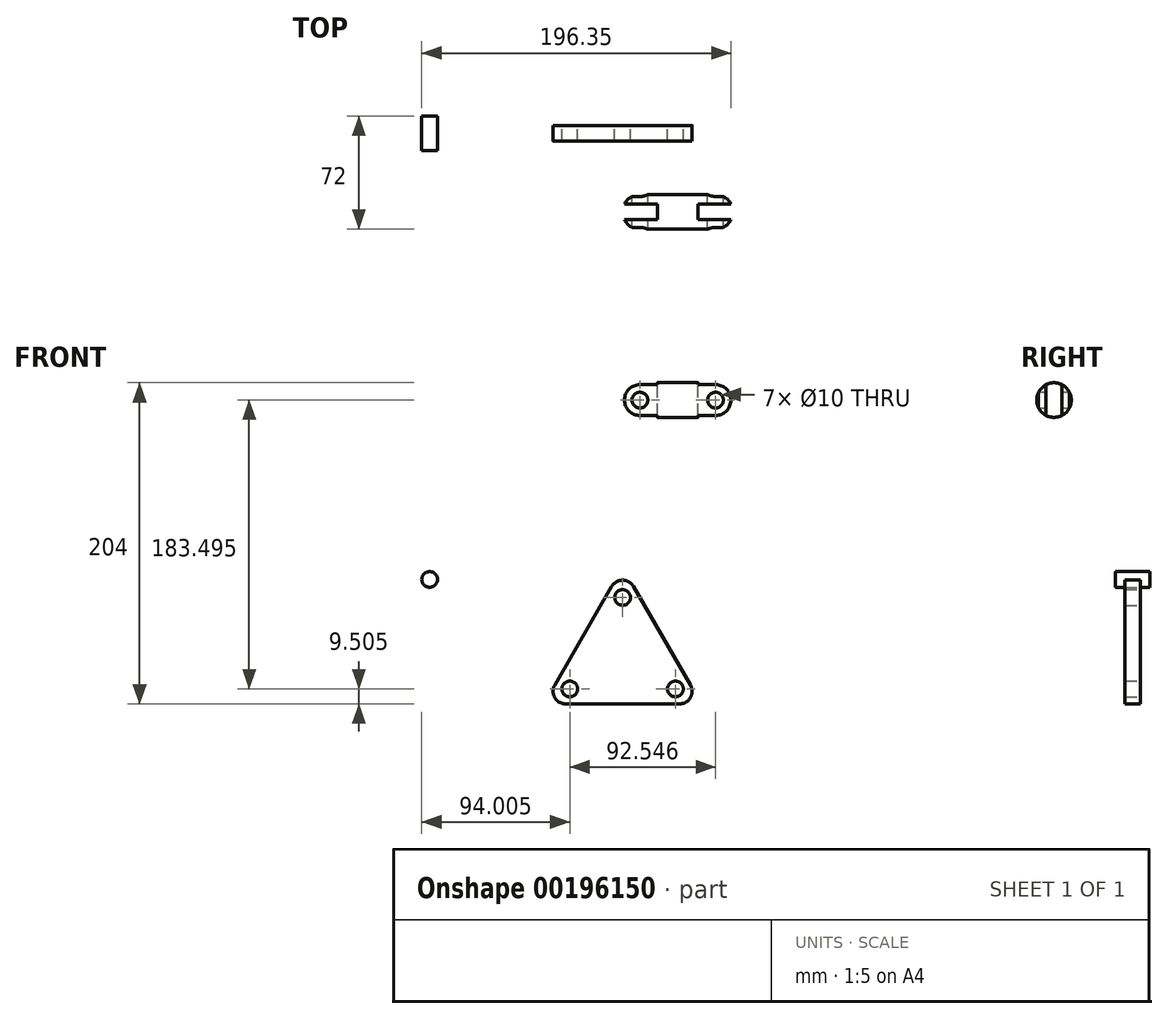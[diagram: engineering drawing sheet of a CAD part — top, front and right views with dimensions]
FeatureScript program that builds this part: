
annotation { "Feature Type Name" : "Feature", "Feature Type Description" : "" }
export const myFeature = defineFeature(function(context is Context, id is Id, definition is map)
    precondition{}
    {
        {
            var Q0;
            Q0=qCreatedBy(makeId("Front.planeOp"),FACE);
            var sketch = newSketch(context, id + "F0", { "sketchPlane" : qUnion([Q0])});
            skLineSegment(sketch, "E0", {"start": v(-36.14, -43) * mm, "end": v(36.14, -43) * mm});
            skLineSegment(sketch, "E1", {"start": v(43.07, -31) * mm, "end": v(6.93, 31.6) * mm});
            skLineSegment(sketch, "E2", {"start": v(-6.93, 31.6) * mm, "end": v(-43.07, -31) * mm});
            skCircle(sketch, "E3", {"center": v(0, 24.6) * mm, "radius": 5 * mm});
            skCircle(sketch, "E4", {"center": v(33.55, -33.5) * mm, "radius": 5 * mm});
            skCircle(sketch, "E5", {"center": v(-33.55, -33.5) * mm, "radius": 5 * mm});
            skPoint(sketch, "E6.visualSharp", {"position": v(0, 43.6) * mm});
            skArc(sketch, "E6.filletArc", {"start": v(6.93, 31.6) * mm, "mid": v(0, 35.6) * mm, "end": v(-6.93, 31.6) * mm});
            skPoint(sketch, "E7.visualSharp", {"position": v(-50, -43) * mm});
            skArc(sketch, "E7.filletArc", {"start": v(-43.07, -31) * mm, "mid": v(-43.07, -39) * mm, "end": v(-36.14, -43) * mm});
            skPoint(sketch, "E8.visualSharp", {"position": v(50, -43) * mm});
            skArc(sketch, "E8.filletArc", {"start": v(36.14, -43) * mm, "mid": v(43.07, -39) * mm, "end": v(43.07, -31) * mm});
            skSolve(sketch);
        }
        {
            var Q0;
            Q0=makeQuery(id+"F0.imprint","IMPRINT",FACE,{"disambiguationData":[TD([[makeQuery(id+"F0.imprint","IMPRINT",EDGE,{"derivedFrom":sQuery(id+"F0.wireOp",EDGE,"E0")}),1.0]])]});
            extrude(context, id + "F1", {"entities" : qUnion([Q0]), "endBound" : BoundingType.SYMMETRIC, "depth" : 10 * mm});
        }
        {
            var Q0;
            Q0=qCreatedBy(makeId("Right.planeOp"),FACE);
            var sketch = newSketch(context, id + "F2", { "sketchPlane" : qUnion([Q0])});
            skCircle(sketch, "E9", {"center": v(-50, 150) * mm, "radius": 11 * mm});
            skSolve(sketch);
        }
        {
            var Q0;
            Q0=makeQuery(id+"F2.imprint","IMPRINT",FACE,{"disambiguationData":[TD([[makeQuery(id+"F2.imprint","IMPRINT",EDGE,{"derivedFrom":sQuery(id+"F2.wireOp",EDGE,"E9")}),1.0]])]});
            var Q1;
            Q1=sQuery(id+"F2.wireOp",EDGE,"E9");
            extrude(context, id + "F3", {"entities" : qUnion([Q0]), "surfaceEntities" : qUnion([Q1]), "depth" : 70 * mm});
        }
        {
            var Q0;
            Q0=makeQuery(id+"F3.opExtrude","CAP_EDGE",EDGE,{"disambiguationData":[OSD([sQuery(id+"F2.wireOp",EDGE,"E9")])],"isStart":false});
            var Q1;
            Q1=makeQuery(id+"F3.opExtrude","CAP_EDGE",EDGE,{"disambiguationData":[OSD([sQuery(id+"F2.wireOp",EDGE,"E9")])],"isStart":true});
            fillet(context, id + "F4", {"entities" : qUnion([Q0, Q1]), "radius" : 11 * mm, "tangentPropagation" : true, "allowEdgeOverflow" : false});
        }
        {
            var Q0;
            Q0=qCreatedBy(makeId("Front.planeOp"),FACE);
            var sketch = newSketch(context, id + "F5", { "sketchPlane" : qUnion([Q0])});
            skCircle(sketch, "E10", {"center": v(11, 150) * mm, "radius": 5 * mm});
            skSolve(sketch);
        }
        {
            var Q0;
            Q0=makeQuery(id+"F5.imprint","IMPRINT",FACE,{"disambiguationData":[TD([[makeQuery(id+"F5.imprint","IMPRINT",EDGE,{"derivedFrom":sQuery(id+"F5.wireOp",EDGE,"E10")}),1.0]])]});
            var Q1;
            Q1=sQuery(id+"F5.wireOp",EDGE,"E10");
            extrude(context, id + "F6", {"entities" : qUnion([Q0]), "surfaceEntities" : qUnion([Q1]), "endBound" : BoundingType.SYMMETRIC, "depth" : 25 * mm});
        }
        {
            var Q0;
            Q0=makeQuery(id+"F6.opExtrude","SWEPT_BODY",BODY,{"disambiguationData":[OSD([sQuery(id+"F5.wireOp",EDGE,"E10")])]});
            transform(context, id + "F7", {"entities" : qUnion([Q0]), "transformType" : TransformType.TRANSLATION_3D, "dx" : 0 * mm, "dy" : 0 * mm, "dz" : 0 * mm, "makeCopy" : true});
        }
        {
            var Q0;
            Q0=makeQuery(id+"F7.opPattern","COPY",BODY,{"derivedFrom":makeQuery(id+"F6.opExtrude","SWEPT_BODY",BODY,{"disambiguationData":[OSD([sQuery(id+"F5.wireOp",EDGE,"E10")])]}),"instanceName":"1"});
            deleteBodies(context, id + "F8", {"entities" : qUnion([Q0])});
        }
        {
            var Q0;
            Q0=makeQuery(id+"F6.opExtrude","SWEPT_BODY",BODY,{"disambiguationData":[OSD([sQuery(id+"F5.wireOp",EDGE,"E10")])]});
            transform(context, id + "F9", {"entities" : qUnion([Q0]), "transformType" : TransformType.TRANSLATION_3D, "dx" : 0 * mm, "dy" : -50 * mm, "dz" : 0 * mm, "makeCopy" : false});
        }
        {
            var Q0;
            Q0=makeQuery(id+"F6.opExtrude","SWEPT_BODY",BODY,{"disambiguationData":[OSD([sQuery(id+"F5.wireOp",EDGE,"E10")])]});
            transform(context, id + "F10", {"entities" : qUnion([Q0]), "transformType" : TransformType.TRANSLATION_3D, "dx" : 48 * mm, "dy" : 0 * mm, "dz" : 0 * mm, "makeCopy" : true});
        }
        {
            var Q0;
            Q0=makeQuery(id+"F6.opExtrude","SWEPT_BODY",BODY,{"disambiguationData":[OSD([sQuery(id+"F5.wireOp",EDGE,"E10")])]});
            var Q1;
            Q1=makeQuery(id+"F10.opPattern","COPY",BODY,{"derivedFrom":makeQuery(id+"F6.opExtrude","SWEPT_BODY",BODY,{"disambiguationData":[OSD([sQuery(id+"F5.wireOp",EDGE,"E10")])]}),"instanceName":"1"});
            var Q2;
            Q2=makeQuery(id+"F3.opExtrude","SWEPT_BODY",BODY,{"disambiguationData":[OSD([sQuery(id+"F2.wireOp",EDGE,"E9")])]});
            booleanBodies(context, id + "F11", {"operationType" : BooleanOperationType.SUBTRACTION, "tools" : qUnion([Q0, Q1]), "targets" : qUnion([Q2])});
        }
        {
            var Q0;
            Q0=qCreatedBy(makeId("Right.planeOp"),FACE);
            var sketch = newSketch(context, id + "F12", { "sketchPlane" : qUnion([Q0])});
            skLineSegment(sketch, "E11.bottom", {"start": v(-55, 136.53) * mm, "end": v(-45, 136.53) * mm});
            skLineSegment(sketch, "E11.top", {"start": v(-55, 163.47) * mm, "end": v(-45, 163.47) * mm});
            skLineSegment(sketch, "E11.left", {"start": v(-55, 136.53) * mm, "end": v(-55, 163.47) * mm});
            skLineSegment(sketch, "E11.right", {"start": v(-45, 136.53) * mm, "end": v(-45, 163.47) * mm});
            skPoint(sketch, "E11.middle", {"position": v(-50, 150) * mm});
            skSolve(sketch);
        }
        {
            var Q0;
            Q0=makeQuery(id+"F12.imprint","IMPRINT",FACE,{"disambiguationData":[TD([[makeQuery(id+"F12.imprint","IMPRINT",EDGE,{"derivedFrom":sQuery(id+"F12.wireOp",EDGE,"E11.bottom")}),1.0]])]});
            extrude(context, id + "F13", {"entities" : qUnion([Q0]), "depth" : 22 * mm});
        }
        {
            var Q0;
            Q0=makeQuery(id+"F13.opExtrude","SWEPT_BODY",BODY,{"disambiguationData":[OSD([sQuery(id+"F12.wireOp",EDGE,"E11.bottom"),sQuery(id+"F12.wireOp",EDGE,"E11.top"),sQuery(id+"F12.wireOp",EDGE,"E11.left"),sQuery(id+"F12.wireOp",EDGE,"E11.right")])]});
            transform(context, id + "F14", {"entities" : qUnion([Q0]), "transformType" : TransformType.TRANSLATION_3D, "dx" : 48 * mm, "dy" : 0 * mm, "dz" : 0 * mm, "makeCopy" : true});
        }
        {
            var Q0;
            Q0=makeQuery(id+"F13.opExtrude","SWEPT_BODY",BODY,{"disambiguationData":[OSD([sQuery(id+"F12.wireOp",EDGE,"E11.bottom"),sQuery(id+"F12.wireOp",EDGE,"E11.top"),sQuery(id+"F12.wireOp",EDGE,"E11.left"),sQuery(id+"F12.wireOp",EDGE,"E11.right")])]});
            var Q1;
            Q1=makeQuery(id+"F14.opPattern","COPY",BODY,{"derivedFrom":makeQuery(id+"F13.opExtrude","SWEPT_BODY",BODY,{"disambiguationData":[OSD([sQuery(id+"F12.wireOp",EDGE,"E11.bottom"),sQuery(id+"F12.wireOp",EDGE,"E11.top"),sQuery(id+"F12.wireOp",EDGE,"E11.left"),sQuery(id+"F12.wireOp",EDGE,"E11.right")])]}),"instanceName":"1"});
            var Q2;
            Q2=makeQuery(id+"F3.opExtrude","SWEPT_BODY",BODY,{"disambiguationData":[OSD([sQuery(id+"F2.wireOp",EDGE,"E9")])]});
            booleanBodies(context, id + "F15", {"operationType" : BooleanOperationType.SUBTRACTION, "tools" : qUnion([Q0, Q1]), "targets" : qUnion([Q2])});
        }
        {
            var Q0;
            Q0=qCreatedBy(makeId("Front.planeOp"),FACE);
            var sketch = newSketch(context, id + "F16", { "sketchPlane" : qUnion([Q0])});
            skCircle(sketch, "E12", {"center": v(-122.55, 36.06) * mm, "radius": 5 * mm});
            skSolve(sketch);
        }
        {
            var Q0;
            Q0=makeQuery(id+"F16.imprint","IMPRINT",FACE,{"disambiguationData":[TD([[makeQuery(id+"F16.imprint","IMPRINT",EDGE,{"derivedFrom":sQuery(id+"F16.wireOp",EDGE,"E12")}),1.0]])]});
            extrude(context, id + "F17", {"entities" : qUnion([Q0]), "endBound" : BoundingType.SYMMETRIC, "depth" : 22 * mm});
        }
    });
